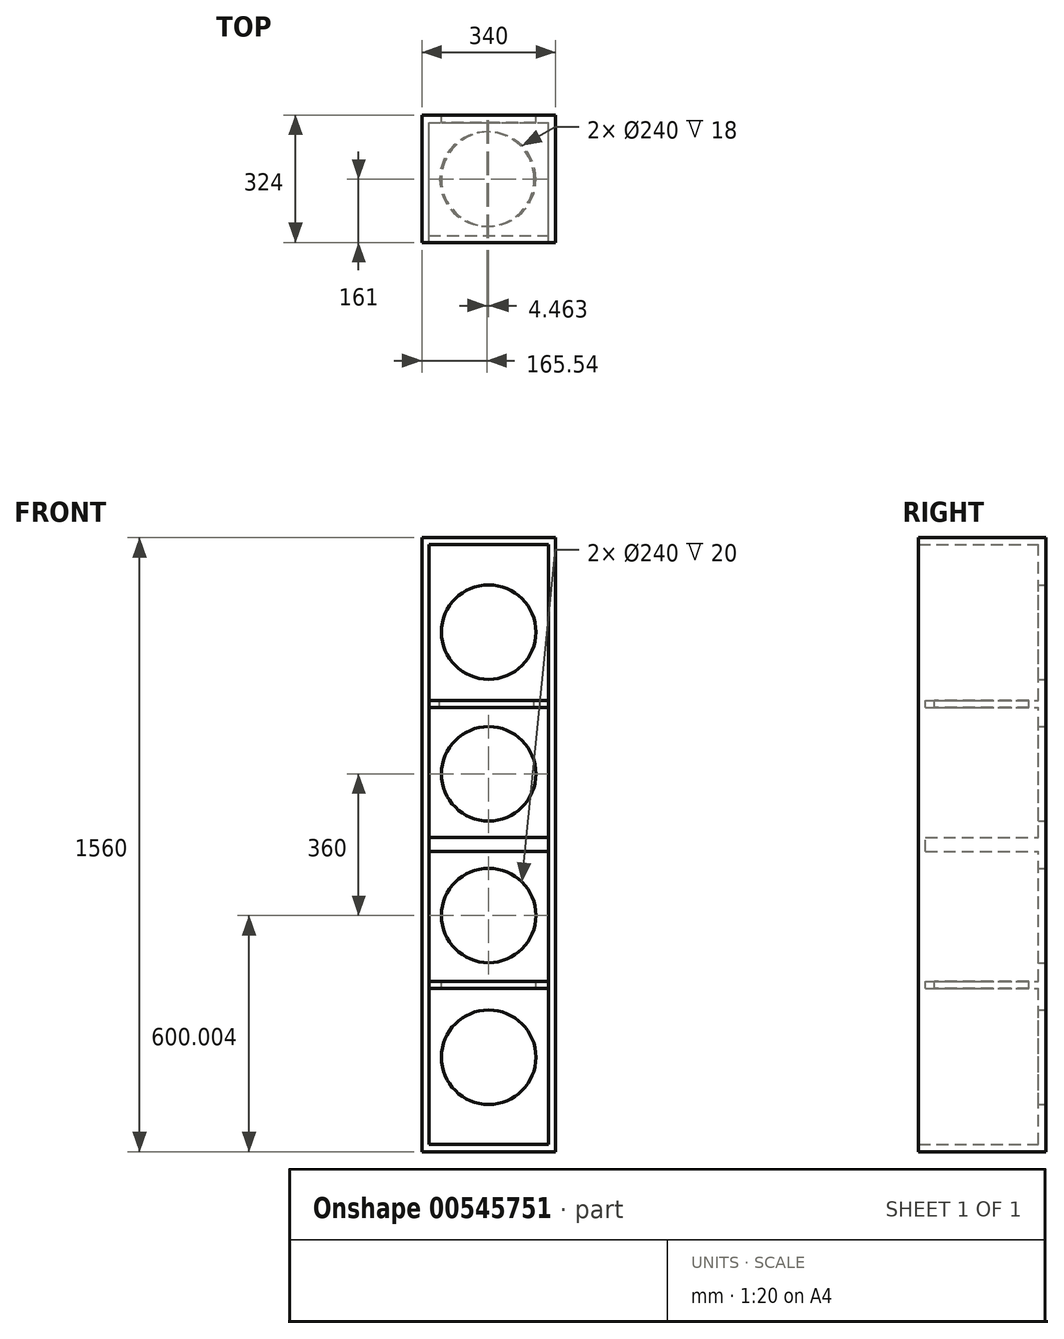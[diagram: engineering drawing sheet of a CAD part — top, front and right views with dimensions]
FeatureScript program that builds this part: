
annotation { "Feature Type Name" : "Feature", "Feature Type Description" : "" }
export const myFeature = defineFeature(function(context is Context, id is Id, definition is map)
    precondition{}
    {
        {
            var Q0;
            Q0=qCreatedBy(makeId("Front.planeOp"),FACE);
            var sketch = newSketch(context, id + "F0", { "sketchPlane" : qUnion([Q0])});
            skLineSegment(sketch, "E0.bottom", {"start": v(-165.54, 779.4) * mm, "end": v(174.46, 779.4) * mm});
            skLineSegment(sketch, "E0.top", {"start": v(-165.54, -780.6) * mm, "end": v(174.46, -780.6) * mm});
            skLineSegment(sketch, "E0.left", {"start": v(-165.54, 779.4) * mm, "end": v(-165.54, -780.6) * mm});
            skLineSegment(sketch, "E0.right", {"start": v(174.46, 779.4) * mm, "end": v(174.46, -780.6) * mm});
            skLineSegment(sketch, "E1", {"start": v(-165.54, -0.6) * mm, "end": v(174.46, -0.6) * mm, "construction": true});
            skCircle(sketch, "E2", {"center": v(4.46, 539.4) * mm, "radius": 120 * mm});
            skCircle(sketch, "E3.0.1.0", {"center": v(4.46, 179.4) * mm, "radius": 120 * mm});
            skCircle(sketch, "E3.0.2.0", {"center": v(4.46, -180.6) * mm, "radius": 120 * mm});
            skCircle(sketch, "E3.0.3.0", {"center": v(4.46, -540.6) * mm, "radius": 120 * mm});
            skLineSegment(sketch, "E3.direction1", {"start": v(4.46, 539.4) * mm, "end": v(29.46, 539.4) * mm, "construction": true});
            skLineSegment(sketch, "E3.direction2", {"start": v(4.46, 539.4) * mm, "end": v(4.46, 179.4) * mm, "construction": true});
            skSolve(sketch);
        }
        {
            var Q0;
            Q0=makeQuery(id+"F0.imprint","IMPRINT",FACE,{"disambiguationData":[TD([[makeQuery(id+"F0.imprint","IMPRINT",EDGE,{"derivedFrom":sQuery(id+"F0.wireOp",EDGE,"E0.bottom")}),-1.0]])]});
            extrude(context, id + "F1", {"entities" : qUnion([Q0]), "depth" : 20 * mm, "offsetDistance" : 25 * mm});
        }
        {
            var Q0;
            Q0=makeQuery(id+"F1.opExtrude","CAP_FACE",FACE,{"disambiguationData":[OSD([sQuery(id+"F0.wireOp",EDGE,"E0.bottom"),sQuery(id+"F0.wireOp",EDGE,"E0.top"),sQuery(id+"F0.wireOp",EDGE,"E0.left"),sQuery(id+"F0.wireOp",EDGE,"E0.right"),sQuery(id+"F0.wireOp",EDGE,"E2"),sQuery(id+"F0.wireOp",EDGE,"E3.0.1.0"),sQuery(id+"F0.wireOp",EDGE,"E3.0.2.0"),sQuery(id+"F0.wireOp",EDGE,"E3.0.3.0")])],"isStart":false});
            var sketch = newSketch(context, id + "F2", { "sketchPlane" : qUnion([Q0])});
            skLineSegment(sketch, "E4.bottom", {"start": v(-165.54, -780.6) * mm, "end": v(-147.54, -780.6) * mm});
            skLineSegment(sketch, "E4.top", {"start": v(-165.54, 779.4) * mm, "end": v(-147.54, 779.4) * mm});
            skLineSegment(sketch, "E4.left", {"start": v(-165.54, -780.6) * mm, "end": v(-165.54, 779.4) * mm});
            skLineSegment(sketch, "E4.right", {"start": v(-147.54, -780.6) * mm, "end": v(-147.54, 779.4) * mm});
            skLineSegment(sketch, "E5.bottom", {"start": v(174.46, -780.6) * mm, "end": v(156.46, -780.6) * mm});
            skLineSegment(sketch, "E5.top", {"start": v(174.46, 779.4) * mm, "end": v(156.46, 779.4) * mm});
            skLineSegment(sketch, "E5.left", {"start": v(174.46, -780.6) * mm, "end": v(174.46, 779.4) * mm});
            skLineSegment(sketch, "E5.right", {"start": v(156.46, -780.6) * mm, "end": v(156.46, 779.4) * mm});
            skLineSegment(sketch, "E6.bottom", {"start": v(156.46, -780.6) * mm, "end": v(-147.54, -780.6) * mm});
            skLineSegment(sketch, "E6.top", {"start": v(156.46, -762.6) * mm, "end": v(-147.54, -762.6) * mm});
            skLineSegment(sketch, "E6.left", {"start": v(156.46, -780.6) * mm, "end": v(156.46, -762.6) * mm});
            skLineSegment(sketch, "E6.right", {"start": v(-147.54, -780.6) * mm, "end": v(-147.54, -762.6) * mm});
            skLineSegment(sketch, "E7.bottom", {"start": v(-147.54, 779.4) * mm, "end": v(156.46, 779.4) * mm});
            skLineSegment(sketch, "E7.top", {"start": v(-147.54, 761.4) * mm, "end": v(156.46, 761.4) * mm});
            skLineSegment(sketch, "E7.left", {"start": v(-147.54, 779.4) * mm, "end": v(-147.54, 761.4) * mm});
            skLineSegment(sketch, "E7.right", {"start": v(156.46, 779.4) * mm, "end": v(156.46, 761.4) * mm});
            skLineSegment(sketch, "E8.bottom", {"start": v(-147.54, 0) * mm, "end": v(156.46, 0) * mm});
            skLineSegment(sketch, "E8.top", {"start": v(-147.54, -18) * mm, "end": v(156.46, -18) * mm});
            skLineSegment(sketch, "E8.left", {"start": v(-147.54, 0) * mm, "end": v(-147.54, -18) * mm});
            skLineSegment(sketch, "E8.right", {"start": v(156.46, 0) * mm, "end": v(156.46, -18) * mm});
            skLineSegment(sketch, "E9.top", {"start": v(-147.54, 18) * mm, "end": v(156.46, 18) * mm});
            skLineSegment(sketch, "E9.left", {"start": v(-147.54, 0) * mm, "end": v(-147.54, 18) * mm});
            skLineSegment(sketch, "E9.right", {"start": v(156.46, 0) * mm, "end": v(156.46, 18) * mm});
            skLineSegment(sketch, "E10.bottom", {"start": v(-147.54, -348) * mm, "end": v(156.46, -348) * mm});
            skLineSegment(sketch, "E10.top", {"start": v(-147.54, -366) * mm, "end": v(156.46, -366) * mm});
            skLineSegment(sketch, "E10.left", {"start": v(-147.54, -348) * mm, "end": v(-147.54, -366) * mm});
            skLineSegment(sketch, "E10.right", {"start": v(156.46, -348) * mm, "end": v(156.46, -366) * mm});
            skLineSegment(sketch, "E11.bottom", {"start": v(-147.54, 348) * mm, "end": v(156.46, 348) * mm});
            skLineSegment(sketch, "E11.top", {"start": v(-147.54, 366) * mm, "end": v(156.46, 366) * mm});
            skLineSegment(sketch, "E11.left", {"start": v(-147.54, 348) * mm, "end": v(-147.54, 366) * mm});
            skLineSegment(sketch, "E11.right", {"start": v(156.46, 348) * mm, "end": v(156.46, 366) * mm});
            skSolve(sketch);
        }
        {
            var Q0;
            Q0=makeQuery(id+"F2.imprint","IMPRINT",FACE,{"disambiguationData":[TD([[makeQuery(id+"F2.imprint","IMPRINT",EDGE,{"derivedFrom":sQuery(id+"F2.wireOp",EDGE,"E4.bottom")}),1.0]])]});
            var Q1;
            Q1=makeQuery(id+"F2.imprint","IMPRINT",FACE,{"disambiguationData":[TD([[makeQuery(id+"F2.imprint","IMPRINT",EDGE,{"derivedFrom":sQuery(id+"F2.wireOp",EDGE,"E7.bottom")}),-1.0]])]});
            var Q2;
            Q2=makeQuery(id+"F2.imprint","IMPRINT",FACE,{"disambiguationData":[TD([[makeQuery(id+"F2.imprint","IMPRINT",EDGE,{"derivedFrom":sQuery(id+"F2.wireOp",EDGE,"E5.bottom")}),1.0]])]});
            var Q3;
            Q3=makeQuery(id+"F2.imprint","IMPRINT",FACE,{"disambiguationData":[TD([[makeQuery(id+"F2.imprint","IMPRINT",EDGE,{"derivedFrom":sQuery(id+"F2.wireOp",EDGE,"E6.bottom")}),1.0]])]});
            extrude(context, id + "F3", {"entities" : qUnion([Q0, Q1, Q2, Q3]), "operationType" : NewBodyOperationType.ADD, "depth" : 304 * mm, "offsetDistance" : 25 * mm});
        }
        {
            var Q0;
            Q0=makeQuery(id+"F2.imprint","IMPRINT",FACE,{"disambiguationData":[TD([[makeQuery(id+"F2.imprint","IMPRINT",EDGE,{"derivedFrom":sQuery(id+"F2.wireOp",EDGE,"E10.bottom")}),-1.0]])]});
            var Q1;
            Q1=makeQuery(id+"F2.imprint","IMPRINT",FACE,{"disambiguationData":[TD([[makeQuery(id+"F2.imprint","IMPRINT",EDGE,{"derivedFrom":sQuery(id+"F2.wireOp",EDGE,"E8.bottom")}),1.0]])]});
            var Q2;
            Q2=makeQuery(id+"F2.imprint","IMPRINT",FACE,{"disambiguationData":[TD([[makeQuery(id+"F2.imprint","IMPRINT",EDGE,{"derivedFrom":sQuery(id+"F2.wireOp",EDGE,"E8.top")}),1.0]])]});
            var Q3;
            Q3=makeQuery(id+"F2.imprint","IMPRINT",FACE,{"disambiguationData":[TD([[makeQuery(id+"F2.imprint","IMPRINT",EDGE,{"derivedFrom":sQuery(id+"F2.wireOp",EDGE,"E11.bottom")}),1.0]])]});
            extrude(context, id + "F4", {"entities" : qUnion([Q0, Q1, Q2, Q3]), "operationType" : NewBodyOperationType.ADD, "depth" : 286 * mm, "offsetDistance" : 25 * mm});
        }
        {
            var Q0;
            Q0=makeQuery(id+"F4.opExtrude","SWEPT_FACE",FACE,{"disambiguationData":[OSD([sQuery(id+"F2.wireOp",EDGE,"E11.top")])]});
            var sketch = newSketch(context, id + "F5", { "sketchPlane" : qUnion([Q0])});
            skCircle(sketch, "E12", {"center": v(0, -163) * mm, "radius": 120 * mm});
            skPoint(sketch, "E12.centerSnap0", {"position": v(156.46, -163) * mm});
            skSolve(sketch);
        }
        {
            var Q0;
            Q0 = qSketchRegion(id + "F5", true);
            extrude(context, id + "F6", {"entities" : qUnion([Q0]), "operationType" : NewBodyOperationType.REMOVE, "oppositeDirection" : true, "depth" : 18 * mm, "offsetDistance" : 25 * mm});
        }
        {
            var Q0;
            Q0=makeQuery(id+"F4.opExtrude","SWEPT_FACE",FACE,{"disambiguationData":[OSD([sQuery(id+"F2.wireOp",EDGE,"E10.bottom")])]});
            var sketch = newSketch(context, id + "F7", { "sketchPlane" : qUnion([Q0])});
            skCircle(sketch, "E13", {"center": v(4.46, -163) * mm, "radius": 120 * mm});
            skPoint(sketch, "E13.centerSnap0", {"position": v(-147.54, -163) * mm});
            skPoint(sketch, "E13.centerSnap1", {"position": v(4.46, -20) * mm});
            skSolve(sketch);
        }
        {
            var Q0;
            Q0 = qSketchRegion(id + "F5", true);
            extrude(context, id + "F8", {"entities" : qUnion([Q0]), "operationType" : NewBodyOperationType.REMOVE, "oppositeDirection" : true, "depth" : 18 * mm, "offsetDistance" : 25 * mm});
        }
        {
            var Q0;
            Q0=makeQuery(id+"F7.imprint","IMPRINT",FACE,{"disambiguationData":[TD([[makeQuery(id+"F7.imprint","IMPRINT",EDGE,{"derivedFrom":sQuery(id+"F7.wireOp",EDGE,"E13")}),1.0]])]});
            var Q1;
            Q1=sQuery(id+"F7.wireOp",EDGE,"E13");
            extrude(context, id + "F9", {"entities" : qUnion([Q0]), "operationType" : NewBodyOperationType.REMOVE, "surfaceEntities" : qUnion([Q1]), "oppositeDirection" : true, "depth" : 18 * mm, "offsetDistance" : 25 * mm});
        }
    });
